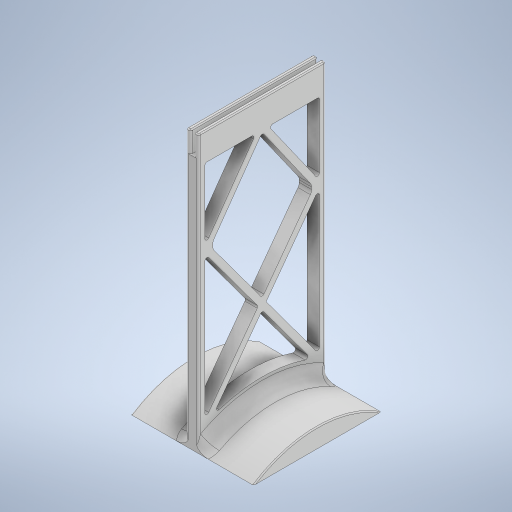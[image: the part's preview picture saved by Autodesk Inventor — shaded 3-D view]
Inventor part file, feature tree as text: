
AUTODESK INVENTOR PART (.ipt)
format: ipt  version: 2023 (Build 270158000, 158)  size: 545,280 bytes
history: native  units: mm
features: fillet x6, extrude x5, sketch x5, plane x1, mirror x1, chamfer x1
ambient origin geometry x8: Origin, YZ Plane, XZ Plane, XY Plane, X Axis, Y Axis, Z Axis, Center Point
bodies: Solid1 (feature_tree)
feature tree (19):
  extrude  "Extrusion1"  Depth=130.0mm
  sketch  "Sketch2"  dims[d2=5.8mm d3=0.0mm d4=60.0mm]
  extrude  "Extrusion2"  Depth=5.8mm
  plane  "Work Plane1"
  mirror  "Mirror1"
  extrude  "Extrusion4"  Depth=26.0mm TaperAngle=0.0deg
  extrude  "Extrusion5"  Depth=10.0mm TaperAngle=0.0deg
  extrude  "Extrusion6"  Depth=3.0mm
  fillet  "Fillet1"  Radius=3.0mm
  fillet  "Fillet2"  Radius=3.0mm
  fillet  "Fillet4"  [1 undecoded]
  chamfer  "Chamfer1"  Angle=45.0deg  [1 undecoded]
  fillet  "Fillet5"  Radius=4.0mm
  fillet  "Fillet6"  [1 undecoded]
  fillet  "Fillet7"  Radius=1.0mm
  sketch  "Sketch1"  dims[d0=60.0mm d1=130.0mm]
  sketch  "Sketch4"  dims[d5=55.0mm d6=26.0mm d7=0.0mm]
  sketch  "Sketch5"  dims[d10=1.8mm d11=10.0mm d12=0.0mm]
  sketch  "Sketch6"  dims[d13=1.0mm d18=3.0mm d19=3.0mm d21=3.0mm d22=45.0deg d23=45.0deg d24=3.0mm d25=3.0mm d26=3.0mm d27=45.0deg d28=45.0deg d29=3.0mm d30=3.0mm d31=3.0mm d32=45.0deg d33=45.0deg d34=4.0mm d35=4.0mm d38=3.0mm d39=3.0mm d40=3.0mm d41=45.0deg d42=45.0deg d43=4.0mm d44=0.0mm d45=0.0mm d47=1.0mm d49=-2.9mm d50=6.0mm d51=0.5mm d52=2.0mm d53=45.0deg d54=0.5mm d55=3.0mm d56=3.0mm d57=16.0mm d58=3.0mm d59=3.0mm d60=3.0mm d61=3.0mm d65=3.0mm d67=26.0mm d68=0.0mm d69=12.0mm d70=65.0mm d71=1.0mm d72=3.0mm d73=3.0mm d74=3.0mm d75=6.0mm d76=34.0mm]
note: 3 required parameter values undecoded (feature->parameter linkage not recoverable at this tier; creation-order binding heuristic only, values carry confidence <= 0.55)
